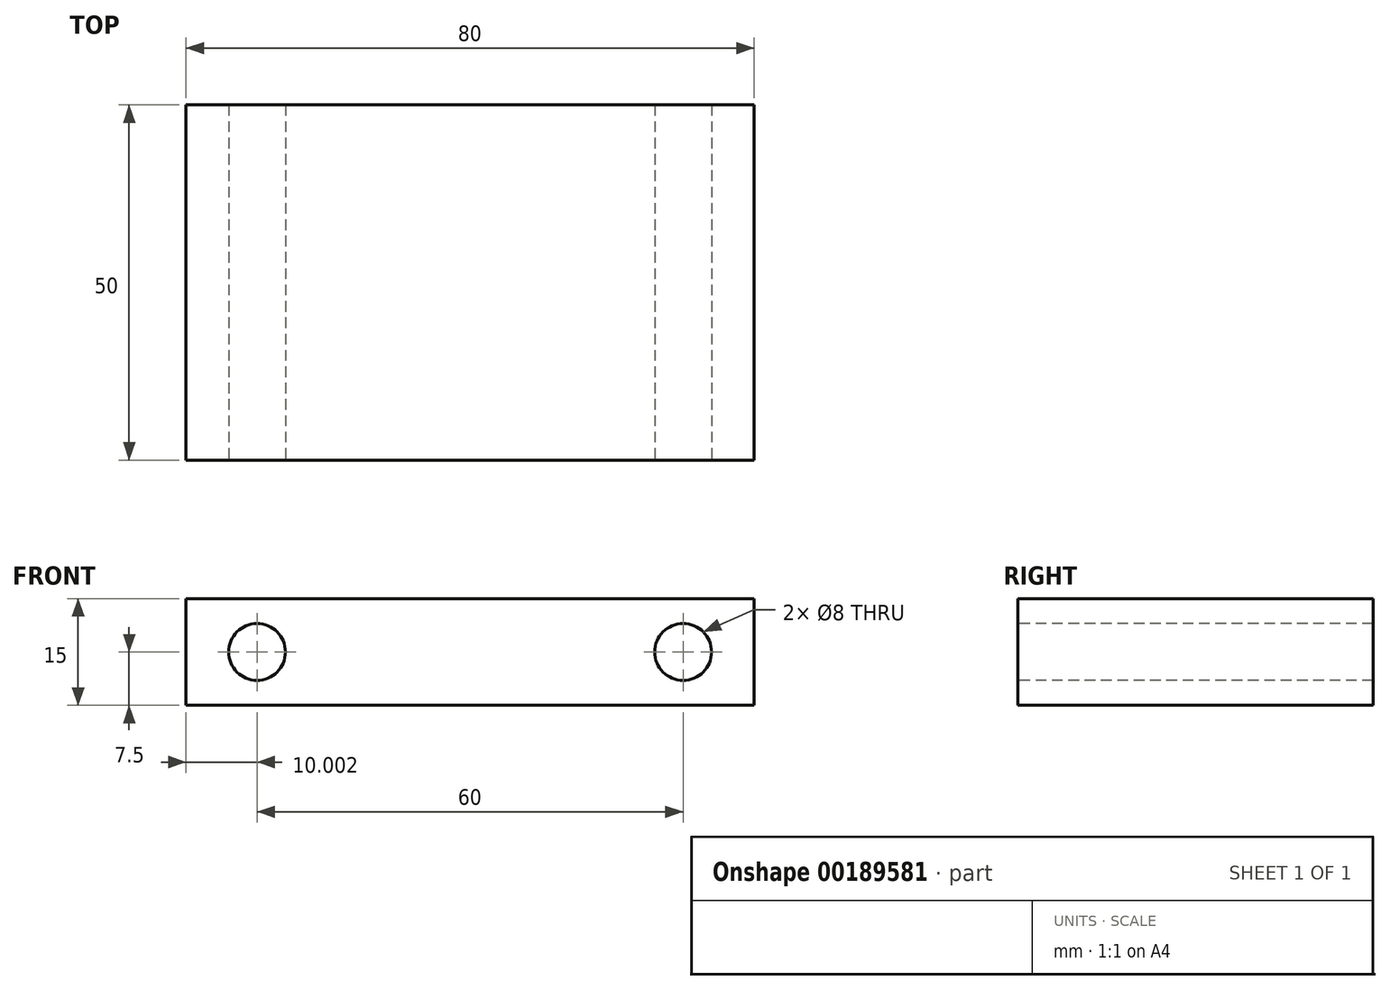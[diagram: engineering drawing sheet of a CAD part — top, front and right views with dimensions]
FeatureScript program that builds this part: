
annotation { "Feature Type Name" : "Feature", "Feature Type Description" : "" }
export const myFeature = defineFeature(function(context is Context, id is Id, definition is map)
    precondition{}
    {
        {
            var Q0;
            Q0=qCreatedBy(makeId("Top.planeOp"),FACE);
            var sketch = newSketch(context, id + "F0", { "sketchPlane" : qUnion([Q0])});
            skLineSegment(sketch, "E0.bottom", {"start": v(-45.7, 25.7) * mm, "end": v(34.3, 25.7) * mm});
            skLineSegment(sketch, "E0.top", {"start": v(-45.7, -24.3) * mm, "end": v(34.3, -24.3) * mm});
            skLineSegment(sketch, "E0.left", {"start": v(-45.7, 25.7) * mm, "end": v(-45.7, -24.3) * mm});
            skLineSegment(sketch, "E0.right", {"start": v(34.3, 25.7) * mm, "end": v(34.3, -24.3) * mm});
            skSolve(sketch);
        }
        {
            var Q0;
            Q0=makeQuery(id+"F0.imprint","IMPRINT",FACE,{"disambiguationData":[TD([[makeQuery(id+"F0.imprint","IMPRINT",EDGE,{"derivedFrom":sQuery(id+"F0.wireOp",EDGE,"E0.bottom")}),-1.0]])]});
            extrude(context, id + "F1", {"entities" : qUnion([Q0]), "depth" : 15 * mm});
        }
        {
            var Q0;
            Q0=makeQuery(id+"F1.opExtrude","SWEPT_FACE",FACE,{"disambiguationData":[OSD([sQuery(id+"F0.wireOp",EDGE,"E0.top")])]});
            var sketch = newSketch(context, id + "F2", { "sketchPlane" : qUnion([Q0])});
            skCircle(sketch, "E1", {"center": v(-35.7, 7.5) * mm, "radius": 4 * mm});
            skCircle(sketch, "E2", {"center": v(24.3, 7.5) * mm, "radius": 4 * mm});
            skSolve(sketch);
        }
        {
            var Q0;
            Q0 = qSketchRegion(id + "F2", true);
            extrude(context, id + "F3", {"entities" : qUnion([Q0]), "operationType" : NewBodyOperationType.REMOVE, "oppositeDirection" : true, "depth" : 50 * mm});
        }
    });
